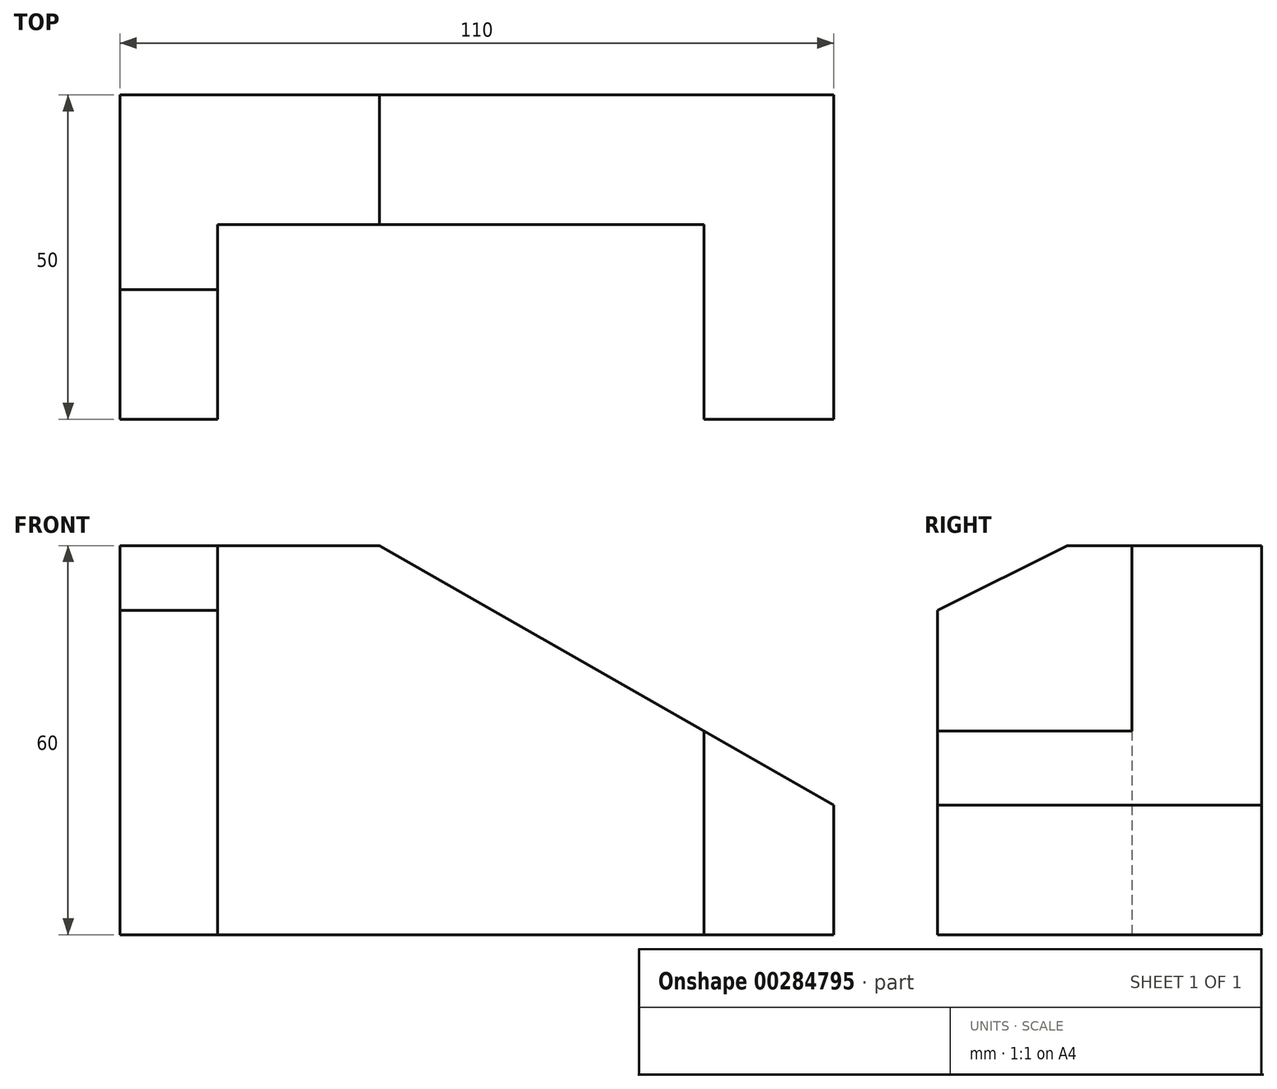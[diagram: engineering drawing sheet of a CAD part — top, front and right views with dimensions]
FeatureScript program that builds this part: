
annotation { "Feature Type Name" : "Feature", "Feature Type Description" : "" }
export const myFeature = defineFeature(function(context is Context, id is Id, definition is map)
    precondition{}
    {
        {
            var Q0;
            Q0=qCreatedBy(makeId("Top.planeOp"),FACE);
            var sketch = newSketch(context, id + "F0", { "sketchPlane" : qUnion([Q0])});
            skLineSegment(sketch, "E0.bottom", {"start": v(-55, -25) * mm, "end": v(-40, -25) * mm});
            skLineSegment(sketch, "E0.top", {"start": v(-55, 25) * mm, "end": v(55, 25) * mm});
            skLineSegment(sketch, "E0.left", {"start": v(-55, -25) * mm, "end": v(-55, 25) * mm});
            skLineSegment(sketch, "E0.right", {"start": v(55, -25) * mm, "end": v(55, 25) * mm});
            skPoint(sketch, "E0.middle", {"position": v(0, 0) * mm});
            skLineSegment(sketch, "E1.top", {"start": v(-40, 5) * mm, "end": v(35, 5) * mm});
            skLineSegment(sketch, "E1.left", {"start": v(-40, -25) * mm, "end": v(-40, 5) * mm});
            skLineSegment(sketch, "E1.right", {"start": v(35, -25) * mm, "end": v(35, 5) * mm});
            skLineSegment(sketch, "E2.trimOffspring", {"start": v(35, -25) * mm, "end": v(55, -25) * mm});
            skSolve(sketch);
        }
        {
            var Q0;
            Q0 = qSketchRegion(id + "F0", true);
            extrude(context, id + "F1", {"entities" : qUnion([Q0]), "depth" : 60 * mm});
        }
        {
            var Q0;
            Q0=makeQuery(id+"F1.opExtrude","CAP_EDGE",EDGE,{"disambiguationData":[OSD([sQuery(id+"F0.wireOp",EDGE,"E0.bottom")])],"isStart":false});
            chamfer(context, id + "F2", {"entities" : qUnion([Q0]), "chamferType" : ChamferType.TWO_OFFSETS, "width1" : 20 * mm, "oppositeDirection" : false, "width2" : 10 * mm, "tangentPropagation" : true});
        }
        {
            var Q0;
            Q0=makeQuery(id+"F1.opExtrude","CAP_EDGE",EDGE,{"disambiguationData":[OSD([sQuery(id+"F0.wireOp",EDGE,"E0.right")])],"isStart":false});
            chamfer(context, id + "F3", {"entities" : qUnion([Q0]), "chamferType" : ChamferType.TWO_OFFSETS, "width1" : 70 * mm, "oppositeDirection" : false, "width2" : 40 * mm, "tangentPropagation" : true});
        }
    });
